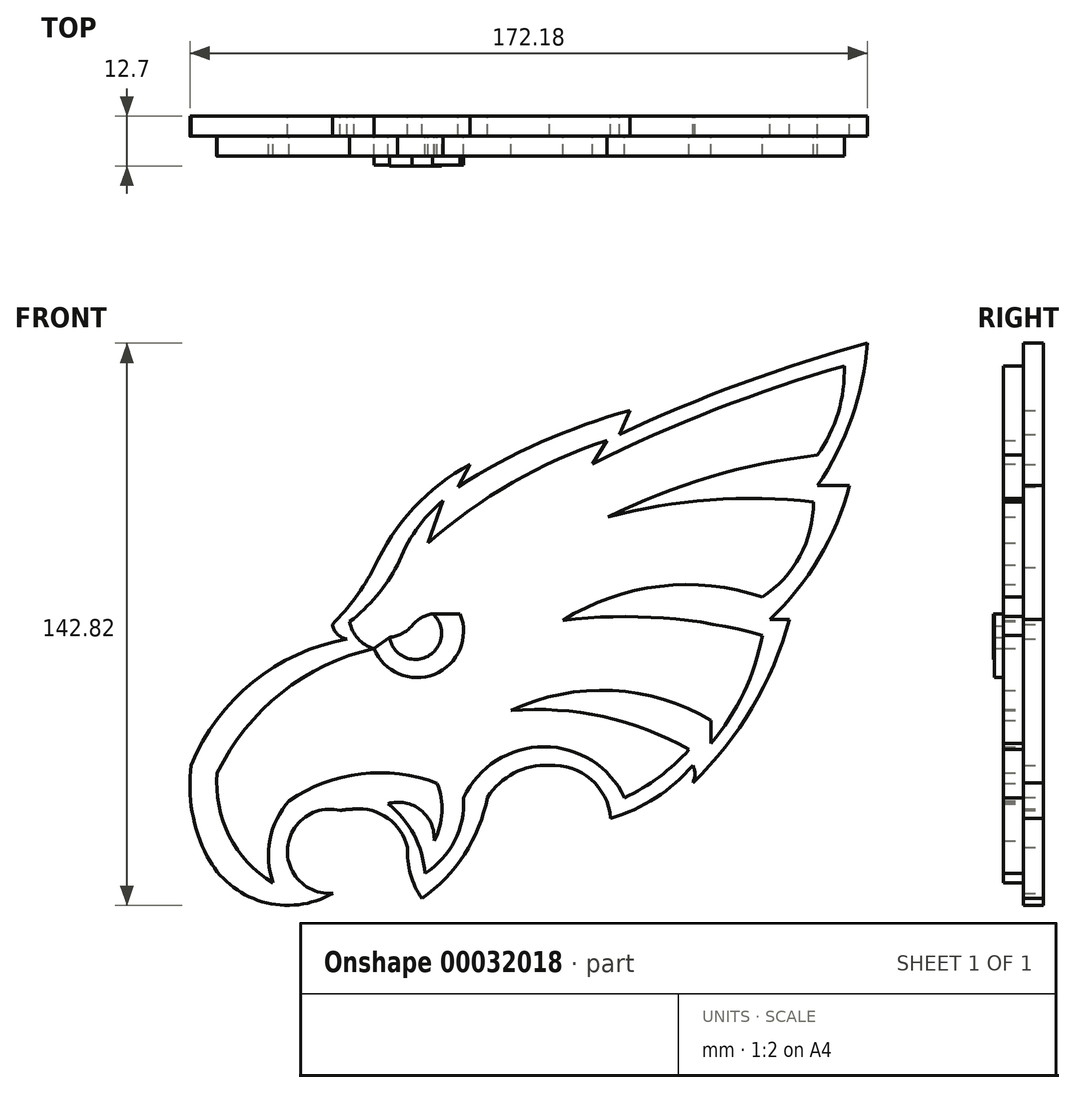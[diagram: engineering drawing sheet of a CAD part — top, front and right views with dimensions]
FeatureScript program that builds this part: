
annotation { "Feature Type Name" : "Feature", "Feature Type Description" : "" }
export const myFeature = defineFeature(function(context is Context, id is Id, definition is map)
    precondition{}
    {
        {
            var Q0;
            Q0=qCreatedBy(makeId("Front.planeOp"),FACE);
            var sketch = newSketch(context, id + "F0", { "sketchPlane" : qUnion([Q0])});
            skArc(sketch, "E0", {"start": v(-8.2, -49.07) * mm, "mid": v(2.58, -37.82) * mm, "end": v(8.44, -23.38) * mm});
            skArc(sketch, "E1", {"start": v(-11.91, -36.1) * mm, "mid": v(-11.1, -42.88) * mm, "end": v(-8.2, -49.07) * mm});
            skArc(sketch, "E2", {"start": v(-11.91, -36.1) * mm, "mid": v(-16.86, -28.64) * mm, "end": v(-25.52, -26.34) * mm});
            skArc(sketch, "E3", {"start": v(-25.52, -26.34) * mm, "mid": v(-27.27, -26.45) * mm, "end": v(-29.01, -26.7) * mm});
            skArc(sketch, "E4", {"start": v(-29.01, -26.7) * mm, "mid": v(-42.35, -36.13) * mm, "end": v(-30.84, -47.72) * mm});
            skPoint(sketch, "E5.startSnap0", {"position": v(-42.35, -36.13) * mm});
            skArc(sketch, "E6", {"start": v(-62.74, -38.33) * mm, "mid": v(-48.8, -49.85) * mm, "end": v(-30.84, -47.72) * mm});
            skArc(sketch, "E7", {"start": v(-27.23, 16.87) * mm, "mid": v(-51.15, 5.93) * mm, "end": v(-66.83, -15.2) * mm});
            skArc(sketch, "E8", {"start": v(24.15, -15.2) * mm, "mid": v(15.2, -17.17) * mm, "end": v(8.44, -23.38) * mm});
            skArc(sketch, "E9", {"start": v(39.74, -28.68) * mm, "mid": v(34.69, -18.76) * mm, "end": v(24.15, -15.2) * mm});
            skArc(sketch, "E10", {"start": v(39.74, -28.68) * mm, "mid": v(51.15, -23.46) * mm, "end": v(60.59, -15.2) * mm});
            skArc(sketch, "E11", {"start": v(60.59, -19.65) * mm, "mid": v(61.12, -17.42) * mm, "end": v(60.59, -15.2) * mm});
            skArc(sketch, "E12", {"start": v(60.59, -19.65) * mm, "mid": v(75.68, -0.58) * mm, "end": v(85.14, 21.81) * mm});
            skLineSegment(sketch, "E13", {"start": v(85.14, 21.81) * mm, "end": v(80.15, 21.81) * mm});
            skArc(sketch, "E14", {"start": v(80.15, 21.81) * mm, "mid": v(92.68, 37.41) * mm, "end": v(100.43, 55.86) * mm});
            skLineSegment(sketch, "E15", {"start": v(100.43, 55.86) * mm, "end": v(92.32, 55.86) * mm});
            skArc(sketch, "E16", {"start": v(92.32, 55.86) * mm, "mid": v(101, 73.13) * mm, "end": v(105, 92.03) * mm});
            skArc(sketch, "E17", {"start": v(-30.97, 20.62) * mm, "mid": v(-29.72, 18.13) * mm, "end": v(-27.23, 16.87) * mm});
            skLineSegment(sketch, "E18", {"start": v(41.96, 68.86) * mm, "end": v(44.61, 74.94) * mm});
            skArc(sketch, "E19", {"start": v(105, 92.03) * mm, "mid": v(72.98, 81.82) * mm, "end": v(41.96, 68.86) * mm});
            skArc(sketch, "E20", {"start": v(44.61, 74.94) * mm, "mid": v(22.05, 66.88) * mm, "end": v(0.93, 55.57) * mm});
            skLineSegment(sketch, "E21", {"start": v(0.93, 55.57) * mm, "end": v(3.97, 61.26) * mm});
            skArc(sketch, "E22", {"start": v(3.97, 61.26) * mm, "mid": v(-10.31, 50.14) * mm, "end": v(-20.34, 35.05) * mm});
            skArc(sketch, "E23", {"start": v(-30.97, 20.62) * mm, "mid": v(-25.1, 27.42) * mm, "end": v(-20.34, 35.05) * mm});
            skPoint(sketch, "E24.start.orphan", {"position": v(60.59, -10.62) * mm});
            skPoint(sketch, "E25.endSnap0", {"position": v(89.02, 39.68) * mm});
            skPoint(sketch, "E26.startSnap0", {"position": v(1.15, -40.94) * mm});
            skPoint(sketch, "E27.center.orphan", {"position": v(-27.71, -43.42) * mm});
            skArc(sketch, "E28", {"start": v(-66.83, -15.2) * mm, "mid": v(-66.57, -27.08) * mm, "end": v(-62.74, -38.33) * mm});
            skSolve(sketch);
        }
        {
            var Q0;
            Q0 = qSketchRegion(id + "F0", true);
            extrude(context, id + "F1", {"entities" : qUnion([Q0]), "depth" : 5.08 * mm});
        }
        {
            var Q0;
            Q0=makeQuery(id+"F1.opExtrude","CAP_FACE",FACE,{"disambiguationData":[OSD([sQuery(id+"F0.wireOp",EDGE,"E0"),sQuery(id+"F0.wireOp",EDGE,"E1"),sQuery(id+"F0.wireOp",EDGE,"E2"),sQuery(id+"F0.wireOp",EDGE,"E3"),sQuery(id+"F0.wireOp",EDGE,"E4"),sQuery(id+"F0.wireOp",EDGE,"E6"),sQuery(id+"F0.wireOp",EDGE,"cad13fe0-b755-493d-871a-a5a57843c18f"),sQuery(id+"F0.wireOp",EDGE,"E7"),sQuery(id+"F0.wireOp",EDGE,"E8"),sQuery(id+"F0.wireOp",EDGE,"E9"),sQuery(id+"F0.wireOp",EDGE,"E10"),sQuery(id+"F0.wireOp",EDGE,"E11"),sQuery(id+"F0.wireOp",EDGE,"E12"),sQuery(id+"F0.wireOp",EDGE,"E13"),sQuery(id+"F0.wireOp",EDGE,"E14"),sQuery(id+"F0.wireOp",EDGE,"E15"),sQuery(id+"F0.wireOp",EDGE,"E16"),sQuery(id+"F0.wireOp",EDGE,"E17"),sQuery(id+"F0.wireOp",EDGE,"E18"),sQuery(id+"F0.wireOp",EDGE,"E19"),sQuery(id+"F0.wireOp",EDGE,"E20"),sQuery(id+"F0.wireOp",EDGE,"E21"),sQuery(id+"F0.wireOp",EDGE,"E22"),sQuery(id+"F0.wireOp",EDGE,"E23")])],"isStart":false});
            var sketch = newSketch(context, id + "F2", { "sketchPlane" : qUnion([Q0])});
            skArc(sketch, "E29", {"start": v(-60.2, -17.14) * mm, "mid": v(-57.18, -33.15) * mm, "end": v(-46.06, -45.05) * mm});
            skArc(sketch, "E30", {"start": v(-41.97, -24.21) * mm, "mid": v(-46.81, -34.08) * mm, "end": v(-46.06, -45.05) * mm});
            skArc(sketch, "E31", {"start": v(-20.39, 14.48) * mm, "mid": v(-43.9, 3.21) * mm, "end": v(-60.2, -17.14) * mm});
            skArc(sketch, "E32", {"start": v(-26.56, 21.28) * mm, "mid": v(-24.46, 16.99) * mm, "end": v(-20.39, 14.48) * mm});
            skArc(sketch, "E33", {"start": v(-26.56, 21.28) * mm, "mid": v(-19.73, 27.85) * mm, "end": v(-14.43, 35.7) * mm});
            skArc(sketch, "E34", {"start": v(-2.9, 52.07) * mm, "mid": v(-9.7, 44.6) * mm, "end": v(-14.43, 35.7) * mm});
            skLineSegment(sketch, "E35", {"start": v(-2.9, 52.07) * mm, "end": v(-6.62, 41.27) * mm});
            skArc(sketch, "E36", {"start": v(38.78, 67.32) * mm, "mid": v(14.76, 56.6) * mm, "end": v(-6.62, 41.27) * mm});
            skLineSegment(sketch, "E37", {"start": v(38.78, 67.32) * mm, "end": v(35.05, 61.37) * mm});
            skArc(sketch, "E38", {"start": v(99.1, 86.3) * mm, "mid": v(66.52, 75.26) * mm, "end": v(35.05, 61.37) * mm});
            skArc(sketch, "E39", {"start": v(92.32, 63.6) * mm, "mid": v(97.54, 74.4) * mm, "end": v(99.1, 86.3) * mm});
            skArc(sketch, "E40", {"start": v(92.32, 63.6) * mm, "mid": v(64.98, 58.06) * mm, "end": v(39.02, 47.84) * mm});
            skArc(sketch, "E41", {"start": v(91.28, 51.7) * mm, "mid": v(64.97, 52.2) * mm, "end": v(39.02, 47.84) * mm});
            skArc(sketch, "E42", {"start": v(78.26, 27.5) * mm, "mid": v(87.82, 37.95) * mm, "end": v(91.28, 51.7) * mm});
            skArc(sketch, "E43", {"start": v(78.26, 27.5) * mm, "mid": v(52.25, 30.28) * mm, "end": v(27.58, 21.62) * mm});
            skArc(sketch, "E44", {"start": v(78.26, 17.83) * mm, "mid": v(53.1, 22.21) * mm, "end": v(27.58, 21.62) * mm});
            skArc(sketch, "E45", {"start": v(65.27, -9.6) * mm, "mid": v(73.56, 3.27) * mm, "end": v(78.26, 17.83) * mm});
            skLineSegment(sketch, "E46", {"start": v(65.27, -9.6) * mm, "end": v(65.27, -3.84) * mm});
            skArc(sketch, "E47", {"start": v(43.28, -23.46) * mm, "mid": v(52.08, -18.14) * mm, "end": v(59.68, -11.22) * mm});
            skPoint(sketch, "E47.startSnap0", {"position": v(51.15, -23.46) * mm});
            skArc(sketch, "E48", {"start": v(43.28, -23.46) * mm, "mid": v(22.81, -10.5) * mm, "end": v(2.35, -23.46) * mm});
            skArc(sketch, "E49", {"start": v(65.27, -3.84) * mm, "mid": v(40.17, 3.81) * mm, "end": v(14.44, -1.32) * mm});
            skArc(sketch, "E50", {"start": v(59.68, -11.22) * mm, "mid": v(37.8, -2.85) * mm, "end": v(14.44, -1.32) * mm});
            skArc(sketch, "E51", {"start": v(-7.46, -42.67) * mm, "mid": v(0.1, -34.42) * mm, "end": v(2.35, -23.46) * mm});
            skArc(sketch, "E52", {"start": v(-7.46, -42.67) * mm, "mid": v(-10.27, -32.8) * mm, "end": v(-16.86, -24.96) * mm});
            skArc(sketch, "E53", {"start": v(-5.1, -34.42) * mm, "mid": v(-8.5, -26.61) * mm, "end": v(-16.86, -24.96) * mm});
            skPoint(sketch, "E53.startSnap0", {"position": v(0.1, -34.42) * mm});
            skArc(sketch, "E54", {"start": v(-5.1, -34.42) * mm, "mid": v(-3.13, -27.17) * mm, "end": v(-4.35, -19.75) * mm});
            skArc(sketch, "E55", {"start": v(-4.35, -19.75) * mm, "mid": v(-23.7, -17.41) * mm, "end": v(-41.97, -24.21) * mm});
            skPoint(sketch, "E56", {"position": v(-16.86, -28.64) * mm});
            skSolve(sketch);
        }
        {
            var Q0;
            Q0 = qSketchRegion(id + "F2", true);
            var Q1;
            Q1=makeQuery(id+"F2.imprint","IMPRINT",FACE,{"disambiguationData":[TD([[makeQuery(id+"F2.imprint","IMPRINT",EDGE,{"derivedFrom":sQuery(id+"F2.wireOp",EDGE,"E29")}),1.0]])]});
            extrude(context, id + "F3", {"entities" : qUnion([Q0, Q1]), "operationType" : NewBodyOperationType.ADD, "depth" : 5.08 * mm});
        }
        {
            var Q0;
            Q0=makeQuery(id+"F3.opExtrude","CAP_FACE",FACE,{"disambiguationData":[OSD([sQuery(id+"F2.wireOp",EDGE,"E29"),sQuery(id+"F2.wireOp",EDGE,"E30"),sQuery(id+"F2.wireOp",EDGE,"E31"),sQuery(id+"F2.wireOp",EDGE,"E32"),sQuery(id+"F2.wireOp",EDGE,"E33"),sQuery(id+"F2.wireOp",EDGE,"E34"),sQuery(id+"F2.wireOp",EDGE,"E35"),sQuery(id+"F2.wireOp",EDGE,"E36"),sQuery(id+"F2.wireOp",EDGE,"E37"),sQuery(id+"F2.wireOp",EDGE,"E38"),sQuery(id+"F2.wireOp",EDGE,"E39"),sQuery(id+"F2.wireOp",EDGE,"E40"),sQuery(id+"F2.wireOp",EDGE,"E41"),sQuery(id+"F2.wireOp",EDGE,"E42"),sQuery(id+"F2.wireOp",EDGE,"E43"),sQuery(id+"F2.wireOp",EDGE,"E44"),sQuery(id+"F2.wireOp",EDGE,"E45"),sQuery(id+"F2.wireOp",EDGE,"E46"),sQuery(id+"F2.wireOp",EDGE,"E47"),sQuery(id+"F2.wireOp",EDGE,"E48"),sQuery(id+"F2.wireOp",EDGE,"E49"),sQuery(id+"F2.wireOp",EDGE,"E50"),sQuery(id+"F2.wireOp",EDGE,"E51"),sQuery(id+"F2.wireOp",EDGE,"E52"),sQuery(id+"F2.wireOp",EDGE,"E53"),sQuery(id+"F2.wireOp",EDGE,"E54"),sQuery(id+"F2.wireOp",EDGE,"E55")])],"isStart":false});
            var sketch = newSketch(context, id + "F4", { "sketchPlane" : qUnion([Q0])});
            skArc(sketch, "E57", {"start": v(-16.42, 17.32) * mm, "mid": v(-13.32, 18.24) * mm, "end": v(-10.76, 20.22) * mm});
            skArc(sketch, "E58", {"start": v(-5.47, 23.28) * mm, "mid": v(-8.4, 22.25) * mm, "end": v(-10.76, 20.22) * mm});
            skArc(sketch, "E59", {"start": v(-16.42, 17.32) * mm, "mid": v(-6.7, 12.5) * mm, "end": v(-5.47, 23.28) * mm});
            skSolve(sketch);
        }
        {
            var Q0;
            Q0=makeQuery(id+"F4.imprint","IMPRINT",FACE,{"disambiguationData":[TD([[makeQuery(id+"F4.imprint","IMPRINT",EDGE,{"derivedFrom":sQuery(id+"F4.wireOp",EDGE,"E57")}),-1.0]])]});
            extrude(context, id + "F5", {"entities" : qUnion([Q0]), "operationType" : NewBodyOperationType.ADD, "depth" : 2.54 * mm});
        }
        {
            var Q0;
            Q0=makeQuery(id+"F3.opExtrude","CAP_FACE",FACE,{"disambiguationData":[OSD([sQuery(id+"F2.wireOp",EDGE,"E29"),sQuery(id+"F2.wireOp",EDGE,"E30"),sQuery(id+"F2.wireOp",EDGE,"E31"),sQuery(id+"F2.wireOp",EDGE,"E32"),sQuery(id+"F2.wireOp",EDGE,"E33"),sQuery(id+"F2.wireOp",EDGE,"E34"),sQuery(id+"F2.wireOp",EDGE,"E35"),sQuery(id+"F2.wireOp",EDGE,"E36"),sQuery(id+"F2.wireOp",EDGE,"E37"),sQuery(id+"F2.wireOp",EDGE,"E38"),sQuery(id+"F2.wireOp",EDGE,"E39"),sQuery(id+"F2.wireOp",EDGE,"E40"),sQuery(id+"F2.wireOp",EDGE,"E41"),sQuery(id+"F2.wireOp",EDGE,"E42"),sQuery(id+"F2.wireOp",EDGE,"E43"),sQuery(id+"F2.wireOp",EDGE,"E44"),sQuery(id+"F2.wireOp",EDGE,"E45"),sQuery(id+"F2.wireOp",EDGE,"E46"),sQuery(id+"F2.wireOp",EDGE,"E47"),sQuery(id+"F2.wireOp",EDGE,"E48"),sQuery(id+"F2.wireOp",EDGE,"E49"),sQuery(id+"F2.wireOp",EDGE,"E50"),sQuery(id+"F2.wireOp",EDGE,"E51"),sQuery(id+"F2.wireOp",EDGE,"E52"),sQuery(id+"F2.wireOp",EDGE,"E53"),sQuery(id+"F2.wireOp",EDGE,"E54"),sQuery(id+"F2.wireOp",EDGE,"E55")])],"isStart":false});
            var sketch = newSketch(context, id + "F6", { "sketchPlane" : qUnion([Q0])});
            skArc(sketch, "E60", {"start": v(-20.39, 14.48) * mm, "mid": v(-5.04, 7.94) * mm, "end": v(1.5, 23.28) * mm});
            skLineSegment(sketch, "E61", {"start": v(-20.39, 14.48) * mm, "end": v(-16.42, 17.32) * mm});
            skLineSegment(sketch, "E62", {"start": v(-5.47, 23.28) * mm, "end": v(1.5, 23.28) * mm});
            skSolve(sketch);
        }
        {
            var Q0;
            Q0 = qSketchRegion(id + "F6", true);
            var Q1;
            Q1=makeQuery(id+"F6.imprint","IMPRINT",FACE,{"disambiguationData":[TD([[makeQuery(id+"F6.imprint","IMPRINT",EDGE,{"derivedFrom":sQuery(id+"F6.wireOp",EDGE,"E60")}),1.0]])]});
            extrude(context, id + "F7", {"entities" : qUnion([Q0, Q1]), "operationType" : NewBodyOperationType.ADD, "depth" : 2.3 * mm});
        }
    });
